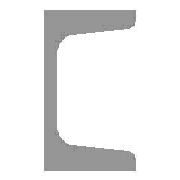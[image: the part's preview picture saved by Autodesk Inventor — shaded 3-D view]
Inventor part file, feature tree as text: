
AUTODESK INVENTOR PART (.ipt)
format: ipt  version: 2017 (Build 210142000, 142)  size: 145,920 bytes
history: native  units: mm (DEFAULTED — no unit token found)
features: other x4, plane x3, split x2, sketch x2
ambient origin geometry x8: Origin, YZ Plane, XZ Plane, XY Plane, X Axis, Y Axis, Z Axis, Center Point
bodies: Solid1 (feature_tree), Body (feature_tree)
feature tree (11):
  parser-record x1  (decoder bookkeeping rows leaked as tree rows — omitted from the tree; the rows remain in map.json)
  other  "Driven Length"
  other  "Start plane"
  other  "End plane"
  plane  "Work Plane4"
  split  "Split1"
  plane  "Work Plane5"
  split  "Split2"
  sketch  "Sketch3"  dims[d0=4.6736mm]
  plane  "Work Plane3"
  sketch  "Sketch4"  dims[d1=50.8mm d2=40.2336mm d3=7.5184mm d4=17.682845mm d5=0.926581mm d6=1219.2mm d7=0.0mm d25=0.0mm d26=-0.0mm d27=1219.2mm d28=6.712646mm d29=2.2352mm d30=90.0deg d31=1219.2mm]
